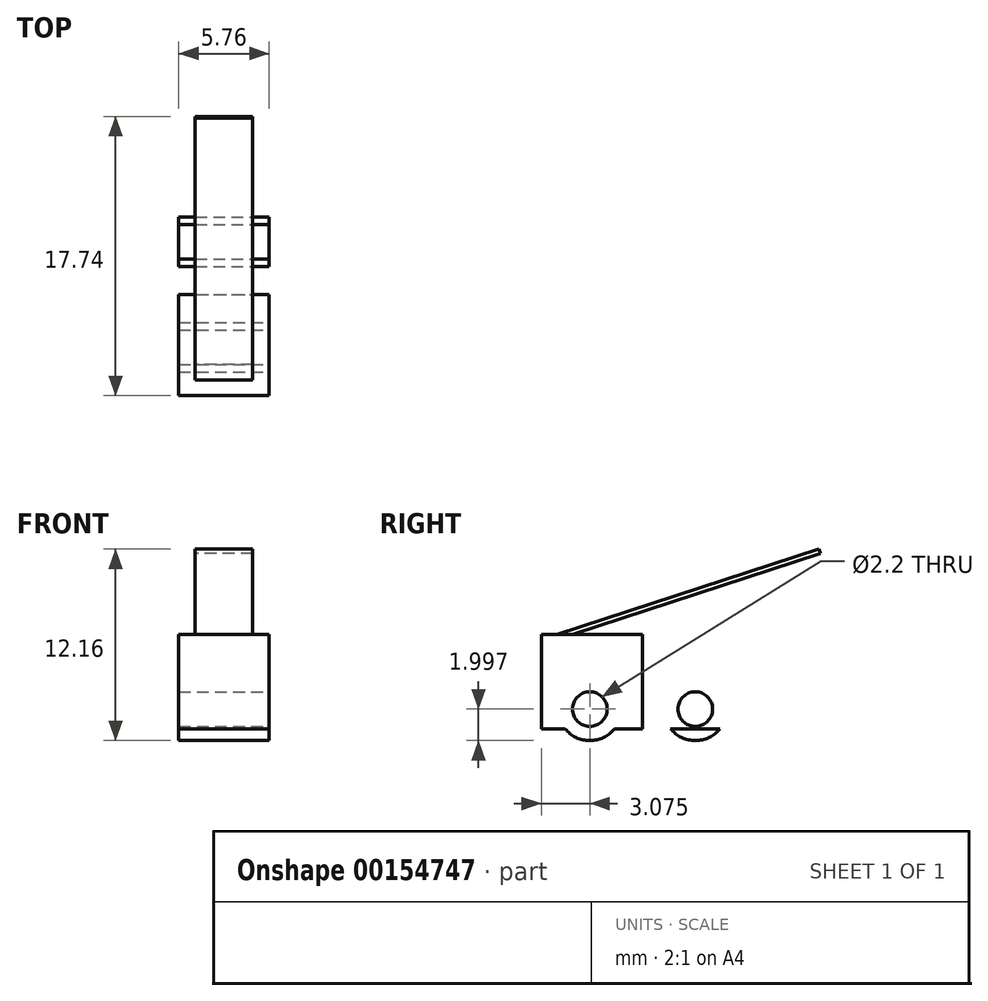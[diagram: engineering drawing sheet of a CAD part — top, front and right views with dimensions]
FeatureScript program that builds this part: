
annotation { "Feature Type Name" : "Feature", "Feature Type Description" : "" }
export const myFeature = defineFeature(function(context is Context, id is Id, definition is map)
    precondition{}
    {
        {
            var Q0;
            Q0=qCreatedBy(makeId("Right.planeOp"),FACE);
            var sketch = newSketch(context, id + "F0", { "sketchPlane" : qUnion([Q0])});
            skLineSegment(sketch, "E0.bottom", {"start": v(0, 0) * mm, "end": v(12.85, 0) * mm});
            skLineSegment(sketch, "E0.top", {"start": v(0, -6) * mm, "end": v(12.85, -6) * mm});
            skLineSegment(sketch, "E0.left", {"start": v(0, 0) * mm, "end": v(0, -6) * mm});
            skLineSegment(sketch, "E0.right", {"start": v(12.85, 0) * mm, "end": v(12.85, -6) * mm});
            skSolve(sketch);
        }
        {
            var Q0;
            Q0 = qSketchRegion(id + "F0", true);
            extrude(context, id + "F1", {"entities" : qUnion([Q0]), "depth" : 5.75 * mm, "symmetric" : true});
        }
        {
            var Q0;
            Q0=makeQuery(id+"F1.opExtrude","CAP_FACE",FACE,{"disambiguationData":[OSD([sQuery(id+"F0.wireOp",EDGE,"E0.bottom"),sQuery(id+"F0.wireOp",EDGE,"E0.top"),sQuery(id+"F0.wireOp",EDGE,"E0.left"),sQuery(id+"F0.wireOp",EDGE,"E0.right")])],"isStart":false});
            var sketch = newSketch(context, id + "F2", { "sketchPlane" : qUnion([Q0])});
            skCircle(sketch, "E1", {"center": v(3.08, -4.75) * mm, "radius": 1.1 * mm});
            skLineSegment(sketch, "E2", {"start": v(6.42, 0) * mm, "end": v(6.42, -6) * mm});
            skCircle(sketch, "E3.MirrorC", {"center": v(9.78, -4.75) * mm, "radius": 1.1 * mm});
            skSolve(sketch);
        }
        {
            var Q0;
            Q0=makeQuery(id+"F2.imprint","IMPRINT",FACE,{"disambiguationData":[TD([[makeQuery(id+"F2.imprint","IMPRINT",EDGE,{"derivedFrom":sQuery(id+"F2.wireOp",EDGE,"E1")}),1.0]])]});
            var Q1;
            Q1=makeQuery(id+"F2.imprint","IMPRINT",FACE,{"disambiguationData":[TD([[makeQuery(id+"F2.imprint","IMPRINT",EDGE,{"derivedFrom":sQuery(id+"F2.wireOp",EDGE,"E3.MirrorC")}),-1.0]])]});
            extrude(context, id + "F3", {"entities" : qUnion([Q0, Q1]), "operationType" : NewBodyOperationType.REMOVE, "oppositeDirection" : true, "depth" : 25 * mm});
        }
        {
            var Q0;
            Q0=makeQuery(id+"F1.opExtrude","CAP_FACE",FACE,{"disambiguationData":[OSD([sQuery(id+"F0.wireOp",EDGE,"E0.bottom"),sQuery(id+"F0.wireOp",EDGE,"E0.top"),sQuery(id+"F0.wireOp",EDGE,"E0.left"),sQuery(id+"F0.wireOp",EDGE,"E0.right")])],"isStart":false});
            var sketch = newSketch(context, id + "F4", { "sketchPlane" : qUnion([Q0])});
            skCircle(sketch, "E4", {"center": v(3.08, -4.75) * mm, "radius": 2 * mm});
            skCircle(sketch, "E5", {"center": v(9.78, -4.75) * mm, "radius": 2 * mm});
            skLineSegment(sketch, "E6", {"start": v(1.51, -6) * mm, "end": v(4.64, -6) * mm});
            skLineSegment(sketch, "E7", {"start": v(4.64, -6) * mm, "end": v(8.21, -6) * mm});
            skLineSegment(sketch, "E8", {"start": v(8.21, -6) * mm, "end": v(11.34, -6) * mm});
            skSolve(sketch);
        }
        {
            var Q0;
            {var subQ0=sQuery(id+"F4.wireOp",EDGE,"E6");Q0=makeQuery(id+"F4.imprint","IMPRINT",FACE,{"disambiguationData":[TD([[makeQuery(id+"F4.imprint","IMPRINT",EDGE,{"derivedFrom":subQ0}),-1.0]])]});}
            var Q1;
            {var subQ0=sQuery(id+"F4.wireOp",EDGE,"E8");Q1=makeQuery(id+"F4.imprint","IMPRINT",FACE,{"disambiguationData":[TD([[makeQuery(id+"F4.imprint","IMPRINT",EDGE,{"derivedFrom":subQ0}),-1.0]])]});}
            extrude(context, id + "F5", {"entities" : qUnion([Q0, Q1]), "operationType" : NewBodyOperationType.ADD, "oppositeDirection" : true, "depth" : 5.75 * mm});
        }
        {
            var Q0;
            Q0=qCreatedBy(makeId("Right.planeOp"),FACE);
            var sketch = newSketch(context, id + "F6", { "sketchPlane" : qUnion([Q0])});
            skLineSegment(sketch, "E9", {"start": v(1, 0) * mm, "end": v(17.64, 5.4) * mm});
            skLineSegment(sketch, "E10", {"start": v(17.64, 5.4) * mm, "end": v(17.74, 5.12) * mm});
            skLineSegment(sketch, "E11", {"start": v(17.74, 5.12) * mm, "end": v(1.97, 0) * mm});
            skLineSegment(sketch, "E12", {"start": v(1.97, 0) * mm, "end": v(1, 0) * mm});
            skSolve(sketch);
        }
        {
            var Q0;
            Q0 = qSketchRegion(id + "F6", true);
            extrude(context, id + "F7", {"entities" : qUnion([Q0]), "operationType" : NewBodyOperationType.ADD, "depth" : 3.65 * mm, "symmetric" : true});
        }
    });
